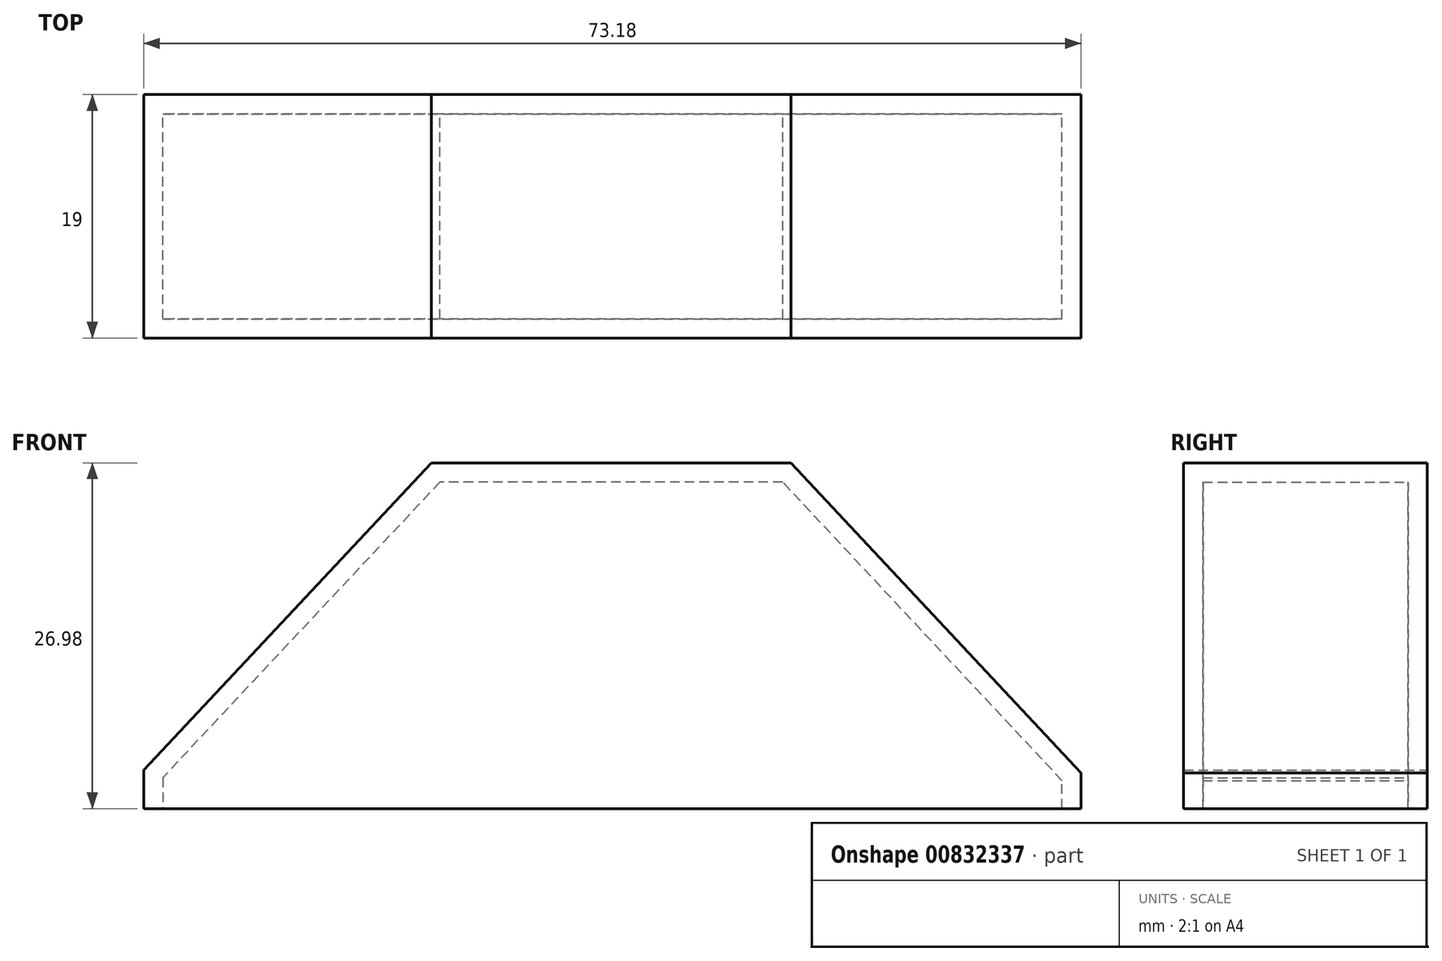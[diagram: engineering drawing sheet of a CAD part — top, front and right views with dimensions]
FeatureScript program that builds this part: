
annotation { "Feature Type Name" : "Feature", "Feature Type Description" : "" }
export const myFeature = defineFeature(function(context is Context, id is Id, definition is map)
    precondition{}
    {
        {
            var Q0;
            Q0=qCreatedBy(makeId("Front.planeOp"),FACE);
            var sketch = newSketch(context, id + "F0", { "sketchPlane" : qUnion([Q0])});
            skLineSegment(sketch, "E0", {"start": v(-36.55, 1.73) * mm, "end": v(-36.55, -1.28) * mm});
            skLineSegment(sketch, "E1", {"start": v(-36.55, -1.28) * mm, "end": v(36.63, -1.28) * mm});
            skLineSegment(sketch, "E2", {"start": v(36.63, -1.28) * mm, "end": v(36.63, 1.5) * mm});
            skLineSegment(sketch, "E3", {"start": v(36.63, 1.5) * mm, "end": v(13.98, 25.7) * mm});
            skLineSegment(sketch, "E4", {"start": v(13.98, 25.7) * mm, "end": v(-14.07, 25.7) * mm});
            skLineSegment(sketch, "E5", {"start": v(-14.07, 25.7) * mm, "end": v(-36.55, 1.73) * mm});
            skSolve(sketch);
        }
        {
            var Q0;
            Q0 = qSketchRegion(id + "F0", true);
            extrude(context, id + "F1", {"entities" : qUnion([Q0]), "depth" : 19 * mm, "offsetDistance" : 25 * mm});
        }
        {
            var Q0;
            Q0=makeQuery(id+"F1.opExtrude","SWEPT_FACE",FACE,{"disambiguationData":[OSD([sQuery(id+"F0.wireOp",EDGE,"E1")])]});
            shell(context, id + "F2", {"entities" : qUnion([Q0]), "thickness" : 1.5 * mm});
        }
    });
